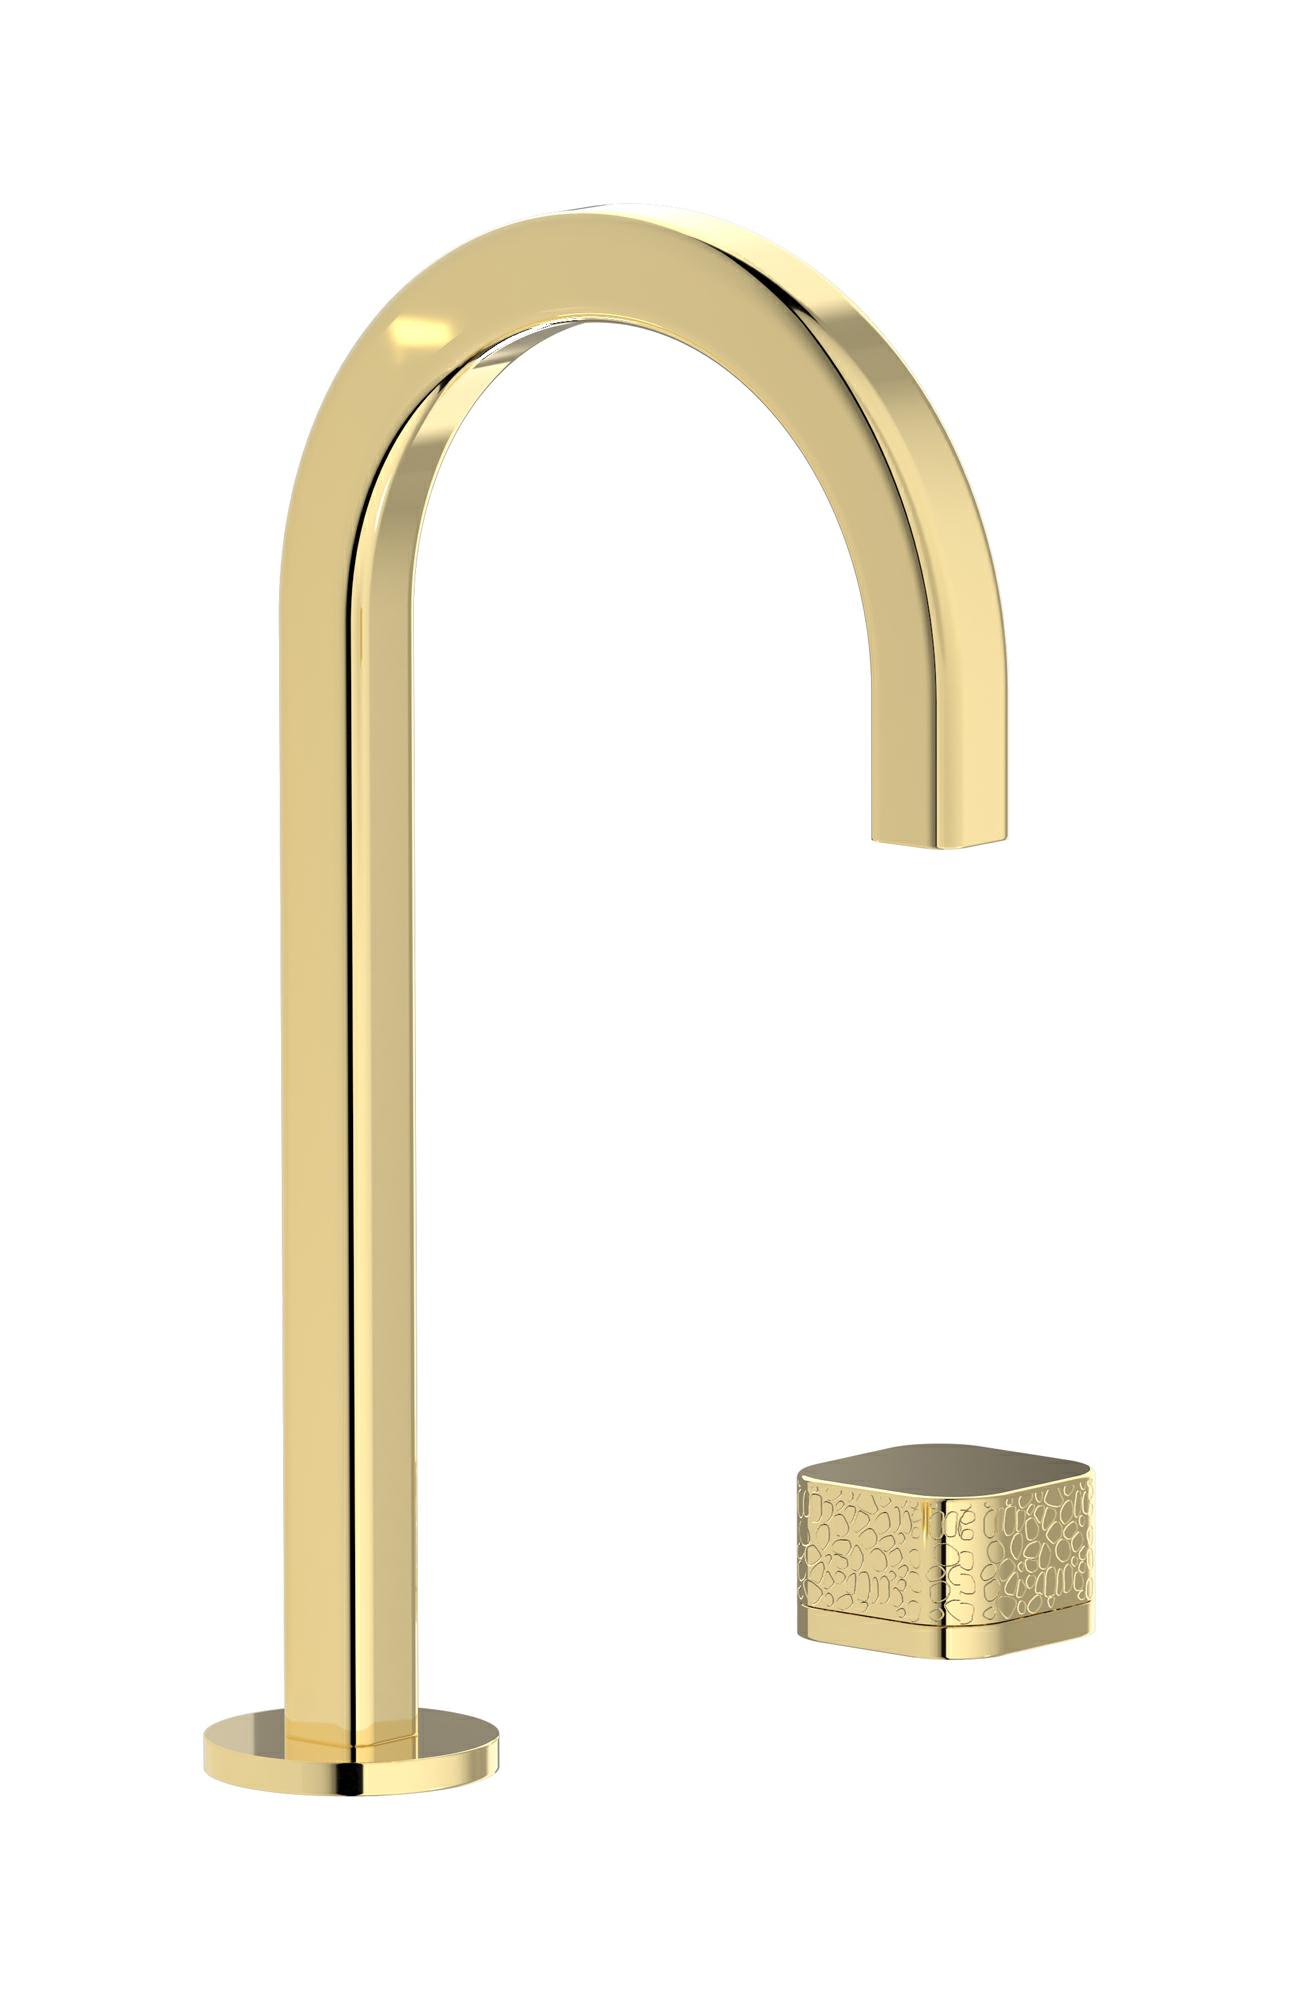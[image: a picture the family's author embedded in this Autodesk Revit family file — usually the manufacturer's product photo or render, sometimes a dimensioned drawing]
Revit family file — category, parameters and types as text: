
# Revit family: EO394_4
name_source: partatom
category: Apparecchi idraulici
units: mm (PartAtom-declared; Revit-internal decimal feet)

## family parameters
Basato su piano di lavoro = No
Condiviso = No
Mantieni orientamento annotazione = No
Numero OmniClass = 23.45.55.17
Punto di calcolo locali = No
Quota connettore circolare = Usa diametro
Sempre verticale = Sì
Taglio con vuoti quando caricato = No
Tipo di parte = Normale
Titolo OmniClass = Mixing Faucets

## types (12) — shared parameters
Cold water inlet = 10 mm  [stored 0.0328084 ft]
Commenti sul tipo = Washbasin
Connessione CW = No
Connessione HW = No
Connessione di scarico = No
Connessione di ventilazione = No
Descrizione = Washbasin two hole mixer
Hot water inlet = 10 mm  [stored 0.0328084 ft]
Produttore = IB Rubinetterie S.p.A.
URL = https://www.weareib.it
zero-valued in all types: Prospetto di default

## per-type parameters (varying)
| type | Finishes surface | Immagine tipo | Modello |
| Chrome | IB_Chrome | EO394CC_4.jpg | EO394CC_4 |
| Brushed nickel | IB_Brushed nickel | EO394SS_4.jpg | EO394SS_4 |
| Matt black | IB_matt black | EO394NP_4.jpg | EO394NP_4 |
| Natural brass | IB_Brass | EO394ON_4.jpg | EO394ON_4 |
| Black chrome | IB_Black chrome | EO394CF_4.jpg | EO394CF_4 |
| Brushed black chrome | IB_Brushed black chrome | EO394CS_4.jpg | EO394CS_4 |
| Pale gold | IB_Pale gold | EO394II_4.jpg | EO394II_4 |
| Brushed pale gold | IB_brushed pale gold | EO394IS_4.jpg | EO394IS_4 |
| Rose gold | IB_Rose gold | EO394RS_4.jpg | EO394RS_4 |
| Brushed rose gold | IB_Brushed rose gold | EO394SR_4.jpg | EO394SR_4 |
| Gold | IB_gold | EO394OO_4.jpg | EO394OO_4 |
| Brushed gold | IB_brushed gold | EO394OS_4.jpg | EO394OS_4 |

note: [stored X ft] marks values corroborated as IEEE doubles in the binary element streams (Revit-internal decimal feet)
